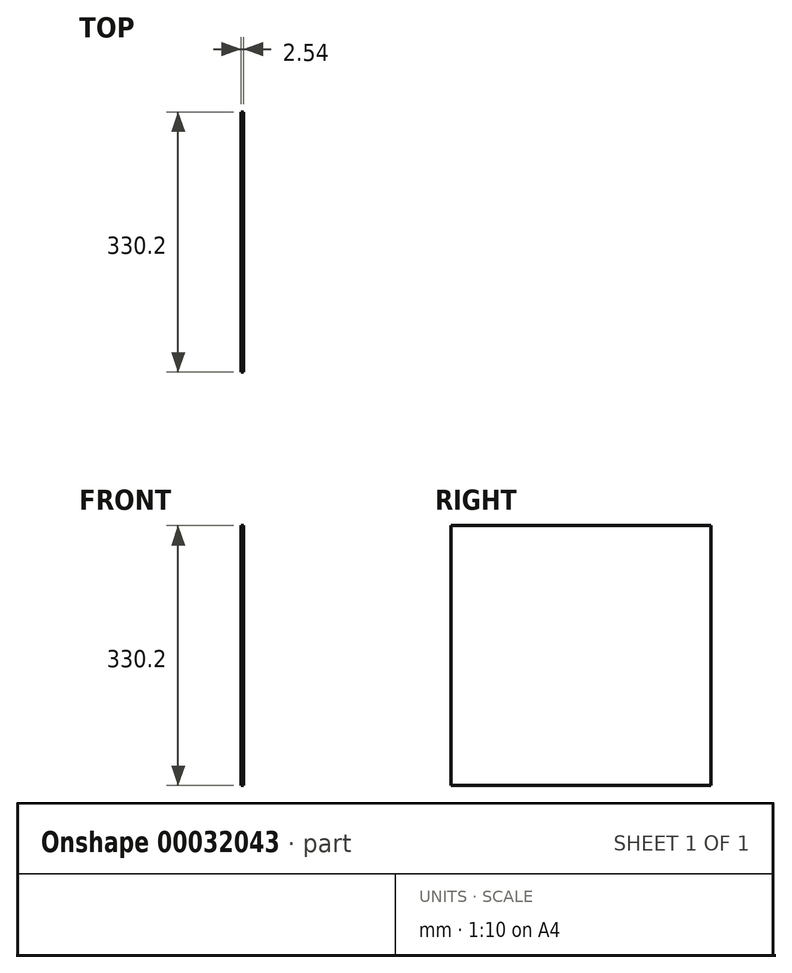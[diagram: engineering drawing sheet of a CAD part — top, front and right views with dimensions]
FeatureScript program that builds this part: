
annotation { "Feature Type Name" : "Feature", "Feature Type Description" : "" }
export const myFeature = defineFeature(function(context is Context, id is Id, definition is map)
    precondition{}
    {
        {
            var Q0;
            Q0=qCreatedBy(makeId("Right.planeOp"),FACE);
            var sketch = newSketch(context, id + "F0", { "sketchPlane" : qUnion([Q0])});
            skLineSegment(sketch, "E0.bottom", {"start": v(165.1, 165.1) * mm, "end": v(-165.1, 165.1) * mm});
            skLineSegment(sketch, "E0.top", {"start": v(165.1, -165.1) * mm, "end": v(-165.1, -165.1) * mm});
            skLineSegment(sketch, "E0.left", {"start": v(165.1, 165.1) * mm, "end": v(165.1, -165.1) * mm});
            skLineSegment(sketch, "E0.right", {"start": v(-165.1, 165.1) * mm, "end": v(-165.1, -165.1) * mm});
            skPoint(sketch, "E0.middle", {"position": v(0, 0) * mm});
            skSolve(sketch);
        }
        {
            var Q0;
            Q0=makeQuery(id+"F0.imprint","IMPRINT",FACE,{"disambiguationData":[TD([[makeQuery(id+"F0.imprint","IMPRINT",EDGE,{"derivedFrom":sQuery(id+"F0.wireOp",EDGE,"E0.bottom")}),1.0]])]});
            extrude(context, id + "F1", {"entities" : qUnion([Q0]), "depth" : 2.54 * mm});
        }
    });
